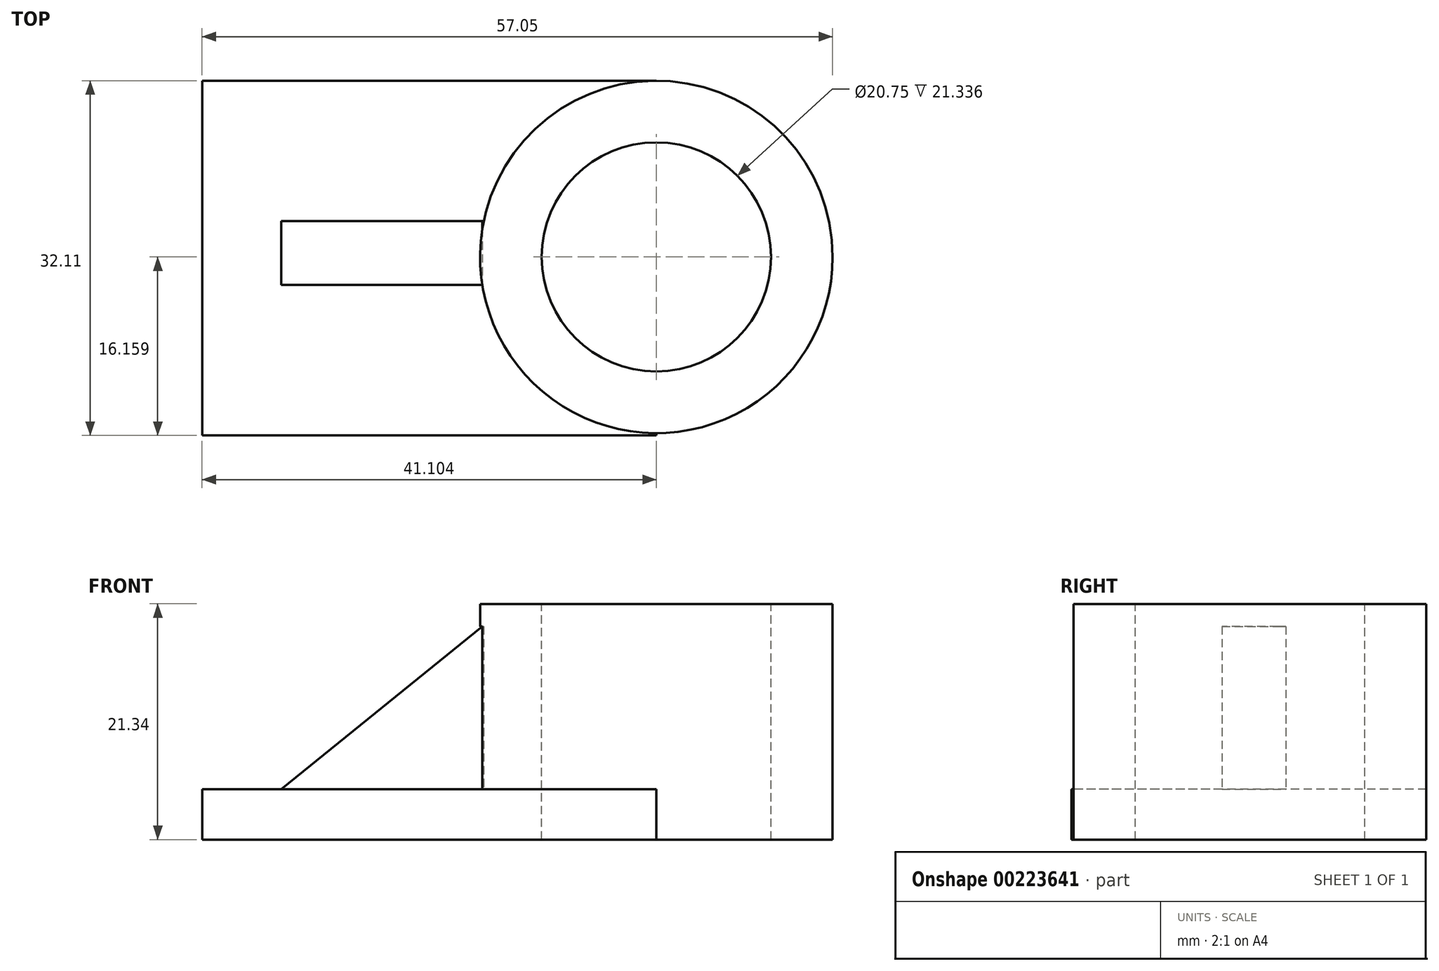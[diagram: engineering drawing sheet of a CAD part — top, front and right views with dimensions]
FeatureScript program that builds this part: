
annotation { "Feature Type Name" : "Feature", "Feature Type Description" : "" }
export const myFeature = defineFeature(function(context is Context, id is Id, definition is map)
    precondition{}
    {
        {
            var Q0;
            Q0=qCreatedBy(makeId("Top.planeOp"),FACE);
            var sketch = newSketch(context, id + "F0", { "sketchPlane" : qUnion([Q0])});
            skCircle(sketch, "E0", {"center": v(31.4, 31.52) * mm, "radius": 15.95 * mm});
            skSolve(sketch);
        }
        {
            var Q0;
            Q0=makeQuery(id+"F0.imprint","IMPRINT",FACE,{"disambiguationData":[TD([[makeQuery(id+"F0.imprint","IMPRINT",EDGE,{"derivedFrom":sQuery(id+"F0.wireOp",EDGE,"E0")}),1.0]])]});
            extrude(context, id + "F1", {"entities" : qUnion([Q0]), "depth" : 21.34 * mm});
        }
        {
            var Q0;
            Q0=makeQuery(id+"F1.opExtrude","CAP_FACE",FACE,{"disambiguationData":[OSD([sQuery(id+"F0.wireOp",EDGE,"E0")])],"isStart":false});
            var sketch = newSketch(context, id + "F2", { "sketchPlane" : qUnion([Q0])});
            skCircle(sketch, "E1", {"center": v(31.4, 31.52) * mm, "radius": 10.37 * mm});
            skSolve(sketch);
        }
        {
            var Q0;
            Q0=makeQuery(id+"F1.opExtrude","CAP_FACE",FACE,{"disambiguationData":[OSD([sQuery(id+"F0.wireOp",EDGE,"E0")])],"isStart":true});
            var sketch = newSketch(context, id + "F3", { "sketchPlane" : qUnion([Q0])});
            skLineSegment(sketch, "E2", {"start": v(31.4, -31.52) * mm, "end": v(31.4, -47.47) * mm});
            skLineSegment(sketch, "E3.bottom", {"start": v(31.4, -47.47) * mm, "end": v(-9.7, -47.47) * mm});
            skLineSegment(sketch, "E3.top", {"start": v(31.4, -15.36) * mm, "end": v(-9.7, -15.36) * mm});
            skLineSegment(sketch, "E3.left", {"start": v(31.4, -47.47) * mm, "end": v(31.4, -15.36) * mm});
            skLineSegment(sketch, "E3.right", {"start": v(-9.7, -47.47) * mm, "end": v(-9.7, -15.36) * mm});
            skSolve(sketch);
        }
        {
            var Q0;
            {var subQ0=sQuery(id+"F3.wireOp",EDGE,"E3.bottom");Q0=makeQuery(id+"F3.imprint","IMPRINT",FACE,{"disambiguationData":[TD([[makeQuery(id+"F3.imprint","IMPRINT",EDGE,{"derivedFrom":subQ0}),-1.0]])]});}
            extrude(context, id + "F4", {"entities" : qUnion([Q0]), "operationType" : NewBodyOperationType.ADD, "oppositeDirection" : true, "depth" : 4.57 * mm});
        }
        {
            var Q0;
            {var subQ0=sQuery(id+"F0.wireOp",EDGE,"E0");Q0=makeQuery(id+"F4.boolean.opBoolean","MERGE",FACE,{"derivedFrom":[makeQuery(id+"F1.opExtrude","CAP_FACE",FACE,{"disambiguationData":[OSD([subQ0])],"isStart":true}),makeQuery(id+"F4.opExtrude","CAP_FACE",FACE,{"disambiguationData":[OSD([subQ0,sQuery(id+"F3.wireOp",EDGE,"E3.bottom"),sQuery(id+"F3.wireOp",EDGE,"E3.top"),sQuery(id+"F3.wireOp",EDGE,"E3.left"),sQuery(id+"F3.wireOp",EDGE,"E3.right")])],"isStart":true})]});}
            var sketch = newSketch(context, id + "F5", { "sketchPlane" : qUnion([Q0])});
            skLineSegment(sketch, "E4.bottom", {"start": v(21.01, -28.98) * mm, "end": v(-2.54, -28.98) * mm});
            skLineSegment(sketch, "E4.top", {"start": v(21.01, -34.75) * mm, "end": v(-2.54, -34.75) * mm});
            skLineSegment(sketch, "E4.left", {"start": v(21.01, -28.98) * mm, "end": v(21.01, -34.75) * mm});
            skLineSegment(sketch, "E4.right", {"start": v(-2.54, -28.98) * mm, "end": v(-2.54, -34.75) * mm});
            skSolve(sketch);
        }
        {
            var Q0;
            Q0=makeQuery(id+"F5.imprint","IMPRINT",FACE,{"disambiguationData":[TD([[makeQuery(id+"F5.imprint","IMPRINT",EDGE,{"derivedFrom":sQuery(id+"F5.wireOp",EDGE,"E4.bottom")}),1.0]])]});
            extrude(context, id + "F6", {"entities" : qUnion([Q0]), "operationType" : NewBodyOperationType.ADD, "oppositeDirection" : true, "depth" : 19.3 * mm});
        }
        {
            var Q0;
            Q0=makeQuery(id+"F6.opExtrude","SWEPT_FACE",FACE,{"disambiguationData":[OSD([sQuery(id+"F5.wireOp",EDGE,"E4.bottom")])]});
            var sketch = newSketch(context, id + "F7", { "sketchPlane" : qUnion([Q0])});
            skLineSegment(sketch, "E5", {"start": v(-2.54, 4.57) * mm, "end": v(15.66, 19.3) * mm});
            skLineSegment(sketch, "E6", {"start": v(15.66, 19.3) * mm, "end": v(-2.54, 19.3) * mm});
            skLineSegment(sketch, "E7", {"start": v(-2.54, 19.3) * mm, "end": v(-2.54, 4.57) * mm});
            skSolve(sketch);
        }
        {
            var Q0;
            Q0 = qSketchRegion(id + "F7", true);
            extrude(context, id + "F8", {"entities" : qUnion([Q0]), "operationType" : NewBodyOperationType.REMOVE, "oppositeDirection" : true, "depth" : 62.23 * mm});
        }
        {
            var Q0;
            Q0=makeQuery(id+"F2.imprint","IMPRINT",FACE,{"disambiguationData":[TD([[makeQuery(id+"F2.imprint","IMPRINT",EDGE,{"derivedFrom":sQuery(id+"F2.wireOp",EDGE,"E1")}),1.0]])]});
            extrude(context, id + "F9", {"entities" : qUnion([Q0]), "operationType" : NewBodyOperationType.REMOVE, "oppositeDirection" : true, "depth" : 47 * mm});
        }
    });
